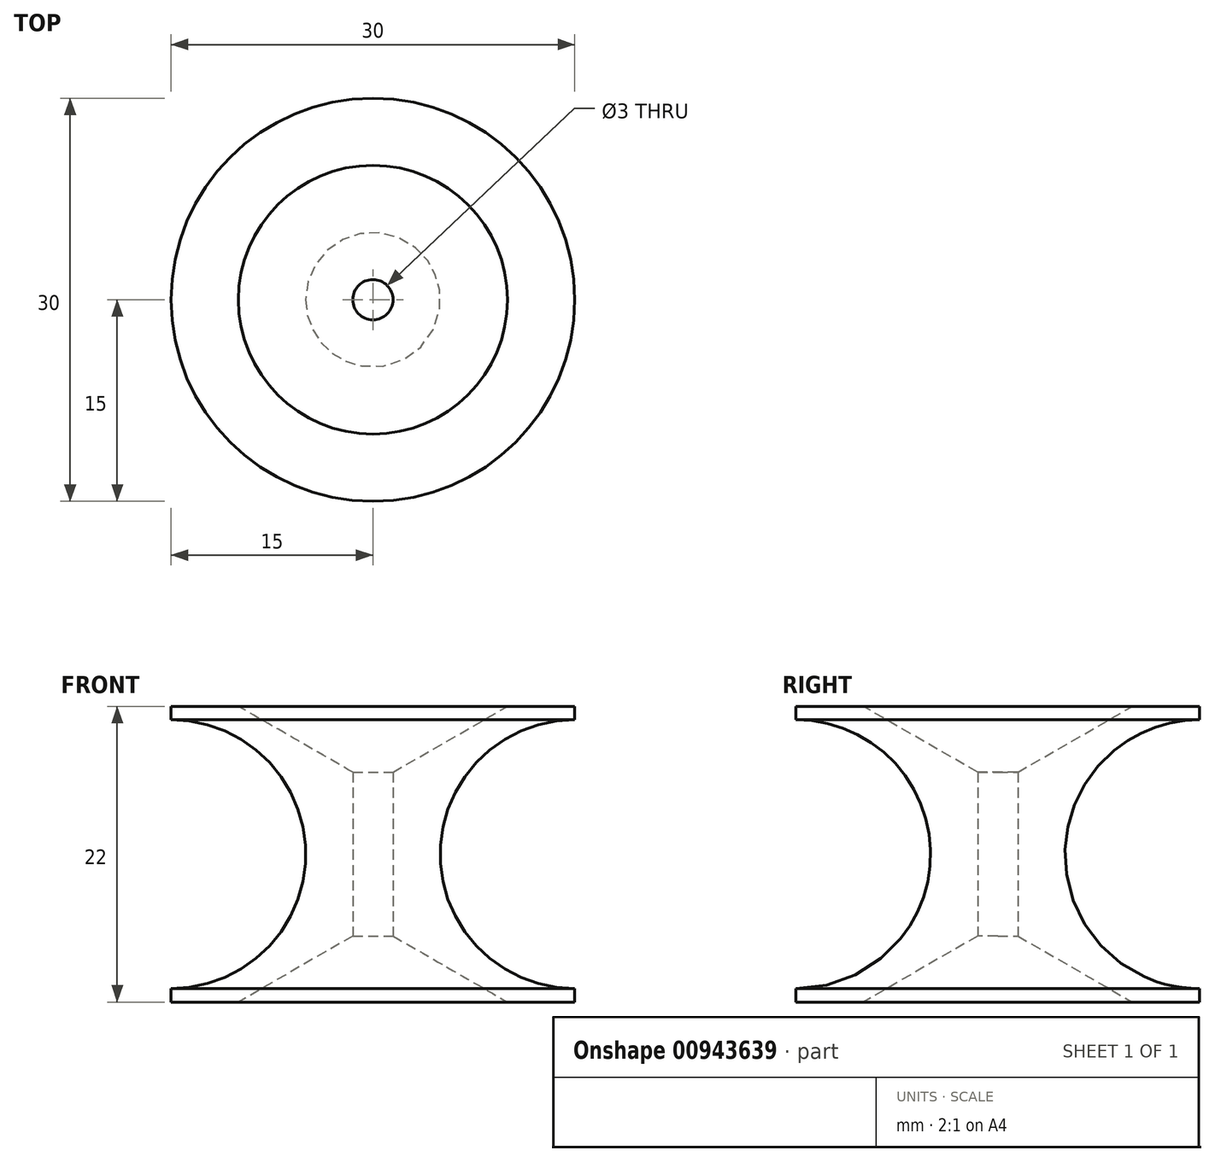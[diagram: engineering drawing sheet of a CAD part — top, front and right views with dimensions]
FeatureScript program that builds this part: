
annotation { "Feature Type Name" : "Feature", "Feature Type Description" : "" }
export const myFeature = defineFeature(function(context is Context, id is Id, definition is map)
    precondition{}
    {
        {
            var Q0;
            Q0=qCreatedBy(makeId("Front.planeOp"),FACE);
            var sketch = newSketch(context, id + "F0", { "sketchPlane" : qUnion([Q0])});
            skArc(sketch, "E0", {"start": v(15, 10) * mm, "mid": v(5, 0) * mm, "end": v(15, -10) * mm});
            skLineSegment(sketch, "E1", {"start": v(15, -10) * mm, "end": v(0, -10) * mm});
            skLineSegment(sketch, "E2", {"start": v(0, 10) * mm, "end": v(15, 10) * mm});
            skPoint(sketch, "E3.start.orphan", {"position": v(0, 0) * mm});
            skLineSegment(sketch, "E4", {"start": v(0, -10) * mm, "end": v(0, 10) * mm});
            skSolve(sketch);
        }
        {
            var Q0;
            Q0=makeQuery(id+"F0.imprint","IMPRINT",FACE,{"disambiguationData":[TD([[makeQuery(id+"F0.imprint","IMPRINT",EDGE,{"derivedFrom":sQuery(id+"F0.wireOp",EDGE,"E0")}),-1.0]])]});
            var Q1;
            Q1=sQuery(id+"F0.wireOp",EDGE,"E4");
            revolve(context, id + "F1", {"surfaceOperationType" : NewSurfaceOperationType.NEW, "entities" : qUnion([Q0]), "axis" : qUnion([Q1]), "revolveType" : RevolveType.FULL});
        }
        {
            var Q0;
            Q0=makeQuery(id+"F1.opRevolve","SWEPT_FACE",FACE,{"disambiguationData":[OSD([sQuery(id+"F0.wireOp",EDGE,"E2")])]});
            extrude(context, id + "F2", {"entities" : qUnion([Q0]), "operationType" : NewBodyOperationType.ADD, "depth" : 1 * mm, "offsetDistance" : 25 * mm});
        }
        {
            var Q0;
            Q0=makeQuery(id+"F1.opRevolve","SWEPT_FACE",FACE,{"disambiguationData":[OSD([sQuery(id+"F0.wireOp",EDGE,"E1")])]});
            extrude(context, id + "F3", {"entities" : qUnion([Q0]), "operationType" : NewBodyOperationType.ADD, "depth" : 1 * mm, "offsetDistance" : 25 * mm});
        }
        {
            var Q0;
            Q0=makeQuery(id+"F2.opExtrude","CAP_FACE",FACE,{"disambiguationData":[OSD([sQuery(id+"F0.wireOp",EDGE,"E2")])],"isStart":false});
            var sketch = newSketch(context, id + "F4", { "sketchPlane" : qUnion([Q0])});
            skPoint(sketch, "E5", {"position": v(0, 0) * mm});
            skSolve(sketch);
        }
        {
            var Q0;
            Q0=sQuery(id+"F4.wireOp",VERTEX,"E5");
            var Q1;
            Q1=makeQuery(id+"F1.opRevolve","SWEPT_BODY",BODY,{"disambiguationData":[OSD([sQuery(id+"F0.wireOp",EDGE,"E0"),sQuery(id+"F0.wireOp",EDGE,"E1"),sQuery(id+"F0.wireOp",EDGE,"E2"),sQuery(id+"F0.wireOp",EDGE,"E4")])]});
            hole(context, id + "F5", {"style" : HoleStyle.C_SINK, "endStyle" : HoleEndStyle.BLIND, "holeDiameter" : 3 * mm, "cSinkDiameter" : 20 * mm, "cSinkAngle" : 120 * degree, "majorDiameter" : 5 * mm, "holeDepth" : 11 * mm, "isTappedThrough" : true, "tappedDepth" : 12 * mm, "tapClearance" : 3, "locations" : qUnion([Q0]), "scope" : qUnion([Q1])});
        }
        {
            var Q0;
            Q0=makeQuery(id+"F3.opExtrude","CAP_FACE",FACE,{"disambiguationData":[OSD([sQuery(id+"F0.wireOp",EDGE,"E1")])],"isStart":false});
            var sketch = newSketch(context, id + "F6", { "sketchPlane" : qUnion([Q0])});
            skPoint(sketch, "E6", {"position": v(0, 0) * mm});
            skSolve(sketch);
        }
        {
            var Q0;
            Q0=sQuery(id+"F6.wireOp",VERTEX,"E6");
            var Q1;
            Q1=makeQuery(id+"F1.opRevolve","SWEPT_BODY",BODY,{"disambiguationData":[OSD([sQuery(id+"F0.wireOp",EDGE,"E0"),sQuery(id+"F0.wireOp",EDGE,"E1"),sQuery(id+"F0.wireOp",EDGE,"E2"),sQuery(id+"F0.wireOp",EDGE,"E4")])]});
            hole(context, id + "F7", {"style" : HoleStyle.C_SINK, "endStyle" : HoleEndStyle.BLIND, "holeDiameter" : 3 * mm, "cSinkDiameter" : 20 * mm, "cSinkAngle" : 120 * degree, "majorDiameter" : 5 * mm, "holeDepth" : 11 * mm, "isTappedThrough" : true, "tappedDepth" : 12 * mm, "tapClearance" : 3, "locations" : qUnion([Q0]), "scope" : qUnion([Q1])});
        }
    });
